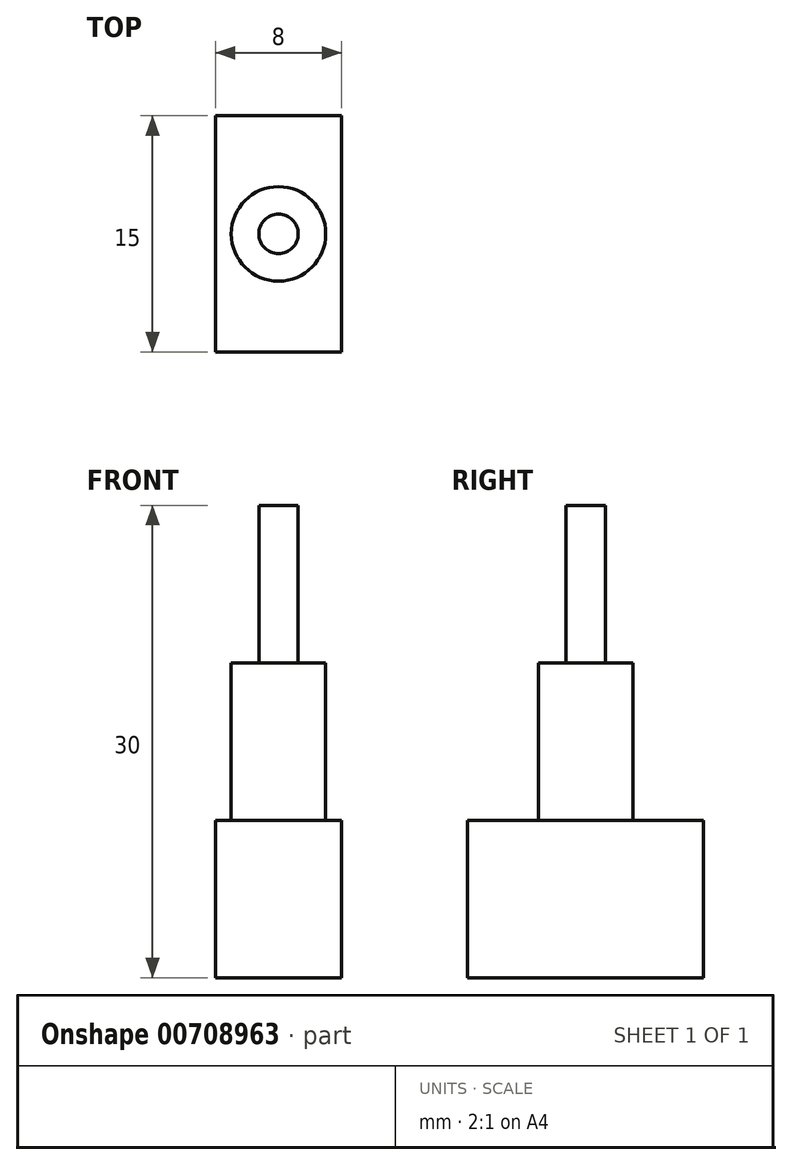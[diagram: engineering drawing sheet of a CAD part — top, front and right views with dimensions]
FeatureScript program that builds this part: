
annotation { "Feature Type Name" : "Feature", "Feature Type Description" : "" }
export const myFeature = defineFeature(function(context is Context, id is Id, definition is map)
    precondition{}
    {
        {
            var Q0;
            Q0=qCreatedBy(makeId("Top.planeOp"),FACE);
            var sketch = newSketch(context, id + "F0", { "sketchPlane" : qUnion([Q0])});
            skLineSegment(sketch, "E0.bottom", {"start": v(-4, 7.5) * mm, "end": v(4, 7.5) * mm});
            skLineSegment(sketch, "E0.top", {"start": v(-4, -7.5) * mm, "end": v(4, -7.5) * mm});
            skLineSegment(sketch, "E0.left", {"start": v(-4, 7.5) * mm, "end": v(-4, -7.5) * mm});
            skLineSegment(sketch, "E0.right", {"start": v(4, 7.5) * mm, "end": v(4, -7.5) * mm});
            skSolve(sketch);
        }
        {
            var Q0;
            Q0 = qSketchRegion(id + "F0", true);
            extrude(context, id + "F1", {"entities" : qUnion([Q0]), "depth" : 10 * mm, "offsetDistance" : 25.4 * mm});
        }
        {
            var Q0;
            Q0=makeQuery(id+"F1.opExtrude","CAP_FACE",FACE,{"disambiguationData":[OSD([sQuery(id+"F0.wireOp",EDGE,"E0.bottom"),sQuery(id+"F0.wireOp",EDGE,"E0.top"),sQuery(id+"F0.wireOp",EDGE,"E0.left"),sQuery(id+"F0.wireOp",EDGE,"E0.right")])],"isStart":false});
            var sketch = newSketch(context, id + "F2", { "sketchPlane" : qUnion([Q0])});
            skCircle(sketch, "E1", {"center": v(0, 0) * mm, "radius": 3 * mm});
            skSolve(sketch);
        }
        {
            var Q0;
            Q0 = qSketchRegion(id + "F2", true);
            extrude(context, id + "F3", {"entities" : qUnion([Q0]), "operationType" : NewBodyOperationType.ADD, "depth" : 10 * mm, "offsetDistance" : 25.4 * mm});
        }
        {
            var Q0;
            Q0=makeQuery(id+"F3.opExtrude","CAP_FACE",FACE,{"disambiguationData":[OSD([sQuery(id+"F2.wireOp",EDGE,"E1")])],"isStart":false});
            var sketch = newSketch(context, id + "F4", { "sketchPlane" : qUnion([Q0])});
            skCircle(sketch, "E2", {"center": v(0, 0) * mm, "radius": 1.25 * mm});
            skSolve(sketch);
        }
        {
            var Q0;
            Q0 = qSketchRegion(id + "F4", true);
            extrude(context, id + "F5", {"entities" : qUnion([Q0]), "operationType" : NewBodyOperationType.ADD, "depth" : 10 * mm, "offsetDistance" : 25.4 * mm});
        }
    });
